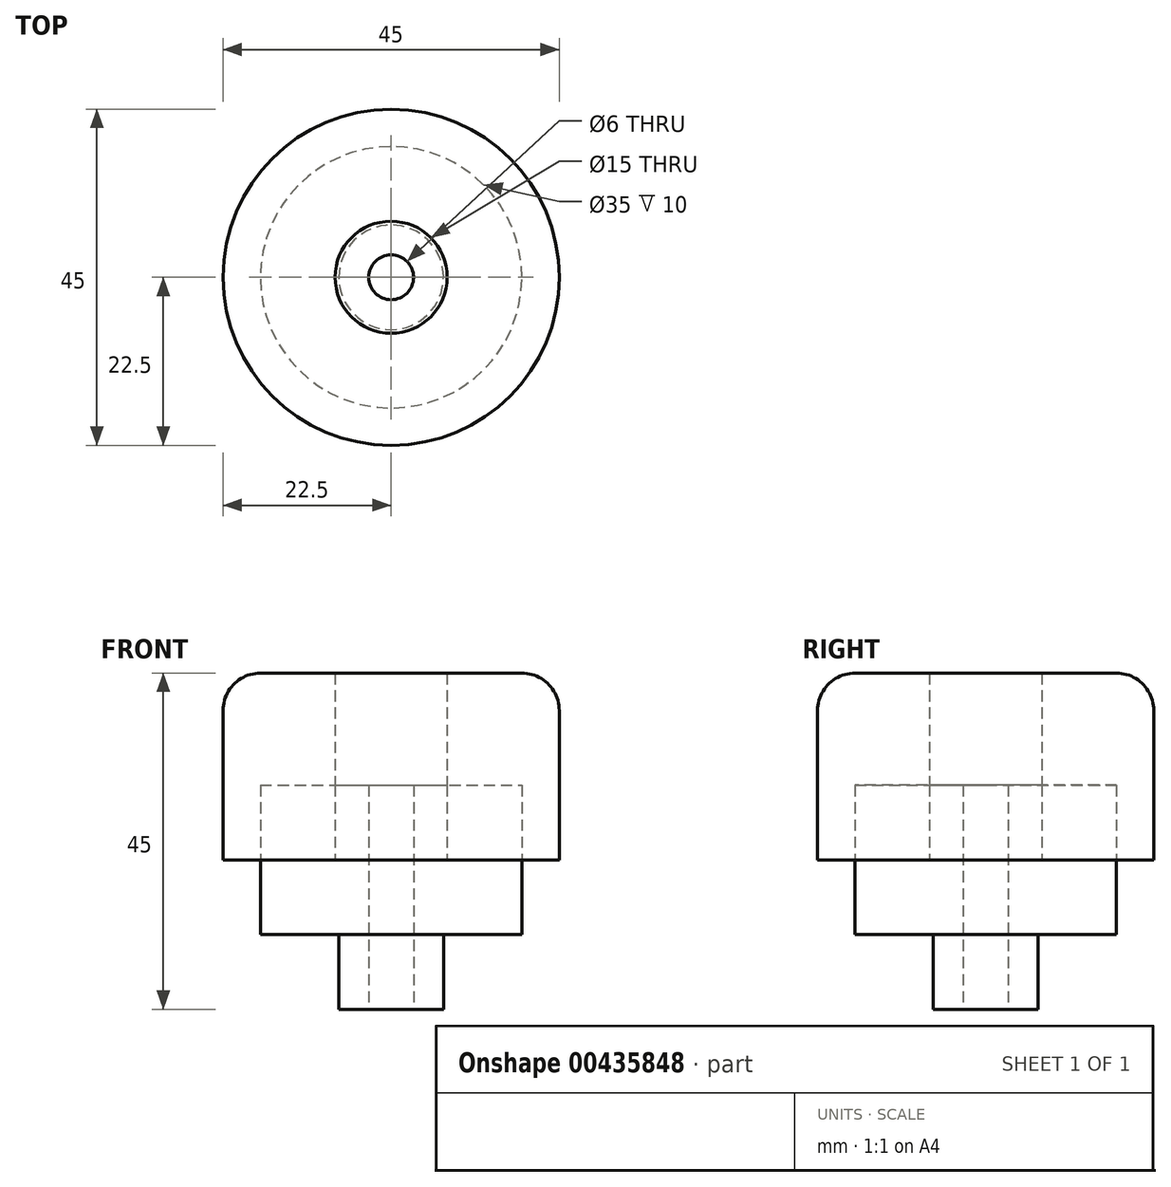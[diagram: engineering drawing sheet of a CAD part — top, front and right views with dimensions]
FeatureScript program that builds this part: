
annotation { "Feature Type Name" : "Feature", "Feature Type Description" : "" }
export const myFeature = defineFeature(function(context is Context, id is Id, definition is map)
    precondition{}
    {
        {
            var Q0;
            Q0=qCreatedBy(makeId("Front.planeOp"),FACE);
            var sketch = newSketch(context, id + "F0", { "sketchPlane" : qUnion([Q0])});
            skLineSegment(sketch, "E0.bottom", {"start": v(0, 0) * mm, "end": v(22.5, 0) * mm});
            skLineSegment(sketch, "E0.top", {"start": v(0, 45) * mm, "end": v(22.5, 45) * mm});
            skLineSegment(sketch, "E0.left", {"start": v(0, 0) * mm, "end": v(0, 45) * mm});
            skLineSegment(sketch, "E0.right", {"start": v(22.5, 0) * mm, "end": v(22.5, 45) * mm});
            skLineSegment(sketch, "E1", {"start": v(3, 45) * mm, "end": v(3, 0) * mm});
            skLineSegment(sketch, "E2", {"start": v(0, 10) * mm, "end": v(22.5, 10) * mm});
            skLineSegment(sketch, "E3", {"start": v(0, 20) * mm, "end": v(22.5, 20) * mm});
            skLineSegment(sketch, "E4", {"start": v(7, 45) * mm, "end": v(7, 0) * mm});
            skLineSegment(sketch, "E5", {"start": v(17.5, 45) * mm, "end": v(17.5, 0) * mm});
            skLineSegment(sketch, "E6", {"start": v(0, 30) * mm, "end": v(22.5, 30) * mm});
            skLineSegment(sketch, "E7", {"start": v(7.5, 45) * mm, "end": v(7.5, 0) * mm});
            skSolve(sketch);
        }
        {
            var Q0;
            {var subQ0=sQuery(id+"F0.wireOp",EDGE,"E5");var subQ1=sQuery(id+"F0.wireOp",EDGE,"E0.top");var subQ2=makeQuery(id+"F0.imprint","INTERSECT",VERTEX,{"derivedFrom":[subQ1,subQ0]});Q0=makeQuery(id+"F0.imprint","IMPRINT",FACE,{"disambiguationData":[TD([[makeQuery(id+"F0.imprint","IMPRINT",EDGE,{"disambiguationData":[TD([[subQ2,1.0]])],"derivedFrom":subQ1}),-1.0]])]});}
            var Q1;
            {var subQ0=sQuery(id+"F0.wireOp",EDGE,"E0.right");var subQ1=sQuery(id+"F0.wireOp",EDGE,"E0.top");var subQ2=makeQuery(id+"F0.imprint","INTERSECT",VERTEX,{"derivedFrom":[subQ1,subQ0]});Q1=makeQuery(id+"F0.imprint","IMPRINT",FACE,{"disambiguationData":[TD([[makeQuery(id+"F0.imprint","IMPRINT",EDGE,{"disambiguationData":[TD([[subQ2,1.0]])],"derivedFrom":subQ1}),-1.0]])]});}
            var Q2;
            {var subQ0=sQuery(id+"F0.wireOp",EDGE,"E3");var subQ1=sQuery(id+"F0.wireOp",EDGE,"E0.right");var subQ2=makeQuery(id+"F0.imprint","INTERSECT",VERTEX,{"derivedFrom":[subQ1,subQ0]});Q2=makeQuery(id+"F0.imprint","IMPRINT",FACE,{"disambiguationData":[TD([[makeQuery(id+"F0.imprint","IMPRINT",EDGE,{"disambiguationData":[TD([[subQ2,-1.0]])],"derivedFrom":subQ1}),1.0]])]});}
            var Q3;
            {var subQ0=sQuery(id+"F0.wireOp",EDGE,"E7");var subQ1=sQuery(id+"F0.wireOp",EDGE,"E2");var subQ2=makeQuery(id+"F0.imprint","INTERSECT",VERTEX,{"derivedFrom":[subQ1,subQ0]});Q3=makeQuery(id+"F0.imprint","IMPRINT",FACE,{"disambiguationData":[TD([[makeQuery(id+"F0.imprint","IMPRINT",EDGE,{"disambiguationData":[TD([[subQ2,-1.0]])],"derivedFrom":subQ1}),1.0]])]});}
            var Q4;
            {var subQ0=sQuery(id+"F0.wireOp",EDGE,"E1");var subQ1=sQuery(id+"F0.wireOp",EDGE,"E0.bottom");var subQ2=makeQuery(id+"F0.imprint","INTERSECT",VERTEX,{"derivedFrom":[subQ1,subQ0]});Q4=makeQuery(id+"F0.imprint","IMPRINT",FACE,{"disambiguationData":[TD([[makeQuery(id+"F0.imprint","IMPRINT",EDGE,{"disambiguationData":[TD([[subQ2,-1.0]])],"derivedFrom":subQ1}),1.0]])]});}
            var Q5;
            {var subQ0=sQuery(id+"F0.wireOp",EDGE,"E4");var subQ1=sQuery(id+"F0.wireOp",EDGE,"E2");var subQ2=makeQuery(id+"F0.imprint","INTERSECT",VERTEX,{"derivedFrom":[subQ1,subQ0]});Q5=makeQuery(id+"F0.imprint","IMPRINT",FACE,{"disambiguationData":[TD([[makeQuery(id+"F0.imprint","IMPRINT",EDGE,{"disambiguationData":[TD([[subQ2,-1.0]])],"derivedFrom":subQ1}),1.0]])]});}
            var Q6;
            {var subQ0=sQuery(id+"F0.wireOp",EDGE,"E4");var subQ1=sQuery(id+"F0.wireOp",EDGE,"E3");var subQ2=makeQuery(id+"F0.imprint","INTERSECT",VERTEX,{"derivedFrom":[subQ1,subQ0]});Q6=makeQuery(id+"F0.imprint","IMPRINT",FACE,{"disambiguationData":[TD([[makeQuery(id+"F0.imprint","IMPRINT",EDGE,{"disambiguationData":[TD([[subQ2,-1.0]])],"derivedFrom":subQ1}),1.0]])]});}
            var Q7;
            {var subQ0=sQuery(id+"F0.wireOp",EDGE,"E6");var subQ1=sQuery(id+"F0.wireOp",EDGE,"E1");var subQ2=makeQuery(id+"F0.imprint","INTERSECT",VERTEX,{"derivedFrom":[subQ1,subQ0]});Q7=makeQuery(id+"F0.imprint","IMPRINT",FACE,{"disambiguationData":[TD([[makeQuery(id+"F0.imprint","IMPRINT",EDGE,{"disambiguationData":[TD([[subQ2,-1.0]])],"derivedFrom":subQ1}),1.0]])]});}
            var Q8;
            {var subQ0=sQuery(id+"F0.wireOp",EDGE,"E3");var subQ1=sQuery(id+"F0.wireOp",EDGE,"E1");var subQ2=makeQuery(id+"F0.imprint","INTERSECT",VERTEX,{"derivedFrom":[subQ1,subQ0]});Q8=makeQuery(id+"F0.imprint","IMPRINT",FACE,{"disambiguationData":[TD([[makeQuery(id+"F0.imprint","IMPRINT",EDGE,{"disambiguationData":[TD([[subQ2,-1.0]])],"derivedFrom":subQ1}),1.0]])]});}
            var Q9;
            Q9=sQuery(id+"F0.wireOp",EDGE,"E0.left");
            revolve(context, id + "F1", {"entities" : qUnion([Q0, Q1, Q2, Q3, Q4, Q5, Q6, Q7, Q8]), "axis" : qUnion([Q9]), "revolveType" : RevolveType.FULL});
        }
        {
            var Q0;
            Q0=makeQuery(id+"F1.opRevolve","SWEPT_EDGE",EDGE,{"disambiguationData":[OSD([sQuery(id+"F0.wireOp",EDGE,"E0.top"),sQuery(id+"F0.wireOp",EDGE,"E0.right")])]});
            fillet(context, id + "F2", {"entities" : qUnion([Q0]), "radius" : 5 * mm, "tangentPropagation" : true, "allowEdgeOverflow" : false});
        }
    });
